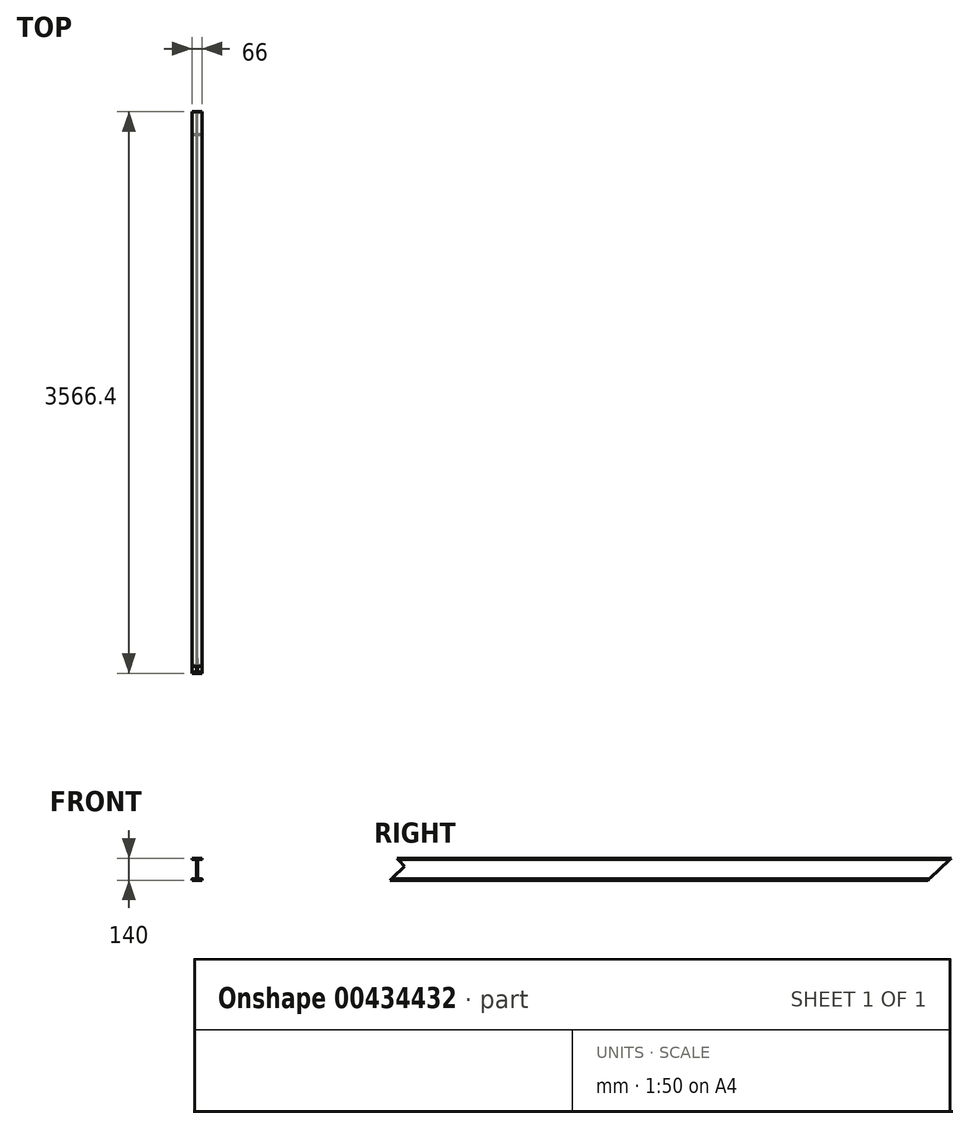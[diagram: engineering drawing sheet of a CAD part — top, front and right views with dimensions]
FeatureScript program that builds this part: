
annotation { "Feature Type Name" : "Feature", "Feature Type Description" : "" }
export const myFeature = defineFeature(function(context is Context, id is Id, definition is map)
    precondition{}
    {
        {
            var Q0;
            Q0=qCreatedBy(makeId("Front.planeOp"),FACE);
            var sketch = newSketch(context, id + "F0", { "sketchPlane" : qUnion([Q0])});
            skLineSegment(sketch, "E0.bottom", {"start": v(-33, 70) * mm, "end": v(33, 70) * mm});
            skLineSegment(sketch, "E0.top", {"start": v(-33, 61.4) * mm, "end": v(-2.85, 61.4) * mm});
            skLineSegment(sketch, "E0.left", {"start": v(-33, 70) * mm, "end": v(-33, 61.4) * mm});
            skLineSegment(sketch, "E0.right", {"start": v(33, 70) * mm, "end": v(33, 61.4) * mm});
            skLineSegment(sketch, "E1.bottom", {"start": v(-33, -61.4) * mm, "end": v(-2.85, -61.4) * mm});
            skLineSegment(sketch, "E1.top", {"start": v(-33, -70) * mm, "end": v(33, -70) * mm});
            skLineSegment(sketch, "E1.left", {"start": v(-33, -61.4) * mm, "end": v(-33, -70) * mm});
            skLineSegment(sketch, "E1.right", {"start": v(33, -61.4) * mm, "end": v(33, -70) * mm});
            skLineSegment(sketch, "E2.left", {"start": v(-2.85, 61.4) * mm, "end": v(-2.85, -61.4) * mm});
            skLineSegment(sketch, "E2.right", {"start": v(2.85, 61.4) * mm, "end": v(2.85, -61.4) * mm});
            skPoint(sketch, "E3.endSnap0", {"position": v(0, -61.4) * mm});
            skLineSegment(sketch, "E4.trimOffspring", {"start": v(2.85, 61.4) * mm, "end": v(33, 61.4) * mm});
            skLineSegment(sketch, "E5.trimOffspring", {"start": v(2.85, -61.4) * mm, "end": v(33, -61.4) * mm});
            skLineSegment(sketch, "E6", {"start": v(0, 70) * mm, "end": v(0, -70) * mm, "construction": true});
            skSolve(sketch);
        }
        {
            var Q0;
            Q0 = qSketchRegion(id + "F0", true);
            extrude(context, id + "F1", {"entities" : qUnion([Q0]), "endBound" : BoundingType.SYMMETRIC, "depth" : 4500 * mm});
        }
        {
            var Q0;
            Q0=qCreatedBy(makeId("Right.planeOp"),FACE);
            var sketch = newSketch(context, id + "F2", { "sketchPlane" : qUnion([Q0])});
            skLineSegment(sketch, "E7", {"start": v(423.93, -1624.17) * mm, "end": v(2250, 70) * mm});
            skLineSegment(sketch, "E8.top", {"start": v(-2250, -1624.17) * mm, "end": v(2250, -1624.17) * mm});
            skLineSegment(sketch, "E8.right", {"start": v(2250, 70) * mm, "end": v(2250, -1624.17) * mm});
            skLineSegment(sketch, "E9", {"start": v(-1300.77, 70) * mm, "end": v(-2250, 70) * mm});
            skLineSegment(sketch, "E10", {"start": v(-2250, 70) * mm, "end": v(-2250, -1624.17) * mm});
            skLineSegment(sketch, "E11", {"start": v(466.6, -1584.58) * mm, "end": v(-1068.46, 70) * mm, "construction": true});
            skLineSegment(sketch, "E12", {"start": v(-1075.59, -70) * mm, "end": v(-1316.4, -70) * mm});
            skLineSegment(sketch, "E13", {"start": v(-1300.77, 70) * mm, "end": v(-1238.2, 2.56) * mm, "construction": true});
            skLineSegment(sketch, "E14", {"start": v(423.93, -1624.17) * mm, "end": v(-1075.59, -70) * mm});
            skLineSegment(sketch, "E15", {"start": v(-1238.2, 2.56) * mm, "end": v(-1316.4, -70) * mm});
            skLineSegment(sketch, "E16", {"start": v(-1238.2, 2.56) * mm, "end": v(-1223.28, 16.4) * mm});
            skPoint(sketch, "E17.endSnap0", {"position": v(-1269.48, 36.28) * mm});
            skLineSegment(sketch, "E18", {"start": v(-1223.28, 16.4) * mm, "end": v(-1273, 70) * mm});
            skLineSegment(sketch, "E19", {"start": v(-1300.77, 70) * mm, "end": v(-1273, 70) * mm});
            skLineSegment(sketch, "E20", {"start": v(-1300.77, 70) * mm, "end": v(423.93, -1624.17) * mm, "construction": true});
            skLineSegment(sketch, "E21", {"start": v(2904.19, 1091.02) * mm, "end": v(2607.19, 1091.02) * mm});
            skLineSegment(sketch, "E22", {"start": v(2607.19, 1091.02) * mm, "end": v(2744.57, 942.94) * mm});
            skLineSegment(sketch, "E23", {"start": v(2744.57, 942.94) * mm, "end": v(2904.19, 1091.02) * mm});
            skSolve(sketch);
        }
        {
            var Q0;
            Q0=makeQuery(id+"F1.opExtrude","SWEPT_EDGE",EDGE,{"disambiguationData":[OSD([sQuery(id+"F0.wireOp",EDGE,"E2.right"),sQuery(id+"F0.wireOp",EDGE,"E4.trimOffspring")])]});
            var Q1;
            Q1=makeQuery(id+"F1.opExtrude","SWEPT_EDGE",EDGE,{"disambiguationData":[OSD([sQuery(id+"F0.wireOp",EDGE,"E0.top"),sQuery(id+"F0.wireOp",EDGE,"E2.left")])]});
            var Q2;
            Q2=makeQuery(id+"F1.opExtrude","SWEPT_EDGE",EDGE,{"disambiguationData":[OSD([sQuery(id+"F0.wireOp",EDGE,"E1.bottom"),sQuery(id+"F0.wireOp",EDGE,"E2.left")])]});
            var Q3;
            Q3=makeQuery(id+"F1.opExtrude","SWEPT_EDGE",EDGE,{"disambiguationData":[OSD([sQuery(id+"F0.wireOp",EDGE,"E2.right"),sQuery(id+"F0.wireOp",EDGE,"E5.trimOffspring")])]});
            fillet(context, id + "F3", {"entities" : qUnion([Q0, Q1, Q2, Q3]), "radius" : 5.7 * mm, "tangentPropagation" : true, "allowEdgeOverflow" : false});
        }
        {
            var Q0;
            Q0 = qSketchRegion(id + "F2", true);
            extrude(context, id + "F4", {"entities" : qUnion([Q0]), "operationType" : NewBodyOperationType.REMOVE, "endBound" : BoundingType.THROUGH_ALL, "oppositeDirection" : true, "depth" : 25 * mm, "hasSecondDirection" : true, "secondDirectionBound" : SecondDirectionBoundingType.THROUGH_ALL, "secondDirectionOppositeDirection" : false, "secondDirectionDepth" : 25 * mm});
        }
        {
            var Q0;
            Q0=makeQuery(id+"F1.opExtrude","SWEPT_EDGE",EDGE,{"disambiguationData":[OSD([sQuery(id+"F0.wireOp",EDGE,"E0.right"),sQuery(id+"F0.wireOp",EDGE,"E4.trimOffspring")])]});
            var Q1;
            Q1=makeQuery(id+"F1.opExtrude","SWEPT_EDGE",EDGE,{"disambiguationData":[OSD([sQuery(id+"F0.wireOp",EDGE,"E0.top"),sQuery(id+"F0.wireOp",EDGE,"E0.left")])]});
            var Q2;
            Q2=makeQuery(id+"F1.opExtrude","SWEPT_EDGE",EDGE,{"disambiguationData":[OSD([sQuery(id+"F0.wireOp",EDGE,"E1.right"),sQuery(id+"F0.wireOp",EDGE,"E5.trimOffspring")])]});
            var Q3;
            Q3=makeQuery(id+"F1.opExtrude","SWEPT_EDGE",EDGE,{"disambiguationData":[OSD([sQuery(id+"F0.wireOp",EDGE,"E1.bottom"),sQuery(id+"F0.wireOp",EDGE,"E1.left")])]});
            fillet(context, id + "F5", {"entities" : qUnion([Q0, Q1, Q2, Q3]), "radius" : 3.4 * mm, "tangentPropagation" : true, "allowEdgeOverflow" : false});
        }
    });
